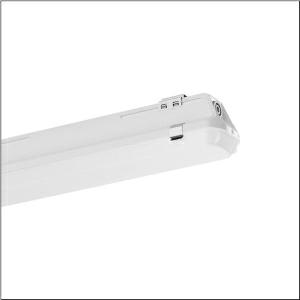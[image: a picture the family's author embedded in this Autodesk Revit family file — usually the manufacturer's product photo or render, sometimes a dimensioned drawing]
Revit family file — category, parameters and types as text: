
# Revit family: monsun_11_51fp108p430h
name_source: partatom
category: Lighting Fixtures
units: mm (PartAtom-declared; Revit-internal decimal feet)

## family parameters
Cut with Voids When Loaded = No
Host = Face
Light Source = No
Part Type = Normal
Room Calculation Point = No
Round Connector Dimension = Use Diameter
Shared = No

## types (1)
- Monsun 11 (1 x LED, 3970 lm, 22.2 W, 4000K)
    Apparent Load = 22 VA
    CIE Flux Codes = 47 77 93 94 100
    Color Rendering = 80
    Color Temperature = 4000K
    Default Elevation = 1800 mm
    Description = Monsun 11, damp-proof luminaire, chain hanger, primary optical cover: enclosure, of PMMA, light emission: direct distribution, primary light characteristic: symmetric, installation type: suspended mounting, surface-mounted, horizontal mounting, vertical mounting, LED, rated luminous flux: 3.970lm, luminous efficacy: 179lm/W, light colour: 840, colour temperature: 4000K, control gear: ON/OFF, with terminal, 3-pole, max. 2.5mm², mains connection: 220..240V, AC, 50/60Hz, rated input power: 22W, luminaire housing, of glass-fibre reinforced polyester, uncoated, bright grey, incl. chain hanger, length: 1.590mm, width: 90mm, height: 88mm, clip for enclosure, of stainless steel (V2A), ceiling mounting element, of stainless steel (V2A), chain hanger, of stainless steel (V2A), protection rating (complete): IP66, insulation class (complete): insulation class I (protective earthing), certification: CE, ENEC, VDE, UKCA, protection symbol: D, impact resistance: IK04, permissible operating ambient temperature: -35..+40°C, standard: EN 50419, EN 60598-2-1, no direct snow, no direct sun, no direct rain, for indoor or canopied outdoor use, corresponds to IFS (International Featured Standards) requirements for safety and quality in the food industry, contact your sales advisor before using the luminaires in applications with unclear chemical exposure, large temperature fluctuations or condensation-forming humidity, LABS conformity tested according to VDMA 24364:2018-05, packaging unit: 1 piece
    Height = 89 mm
    Lamp = 1 x LED
    Lamp Light Flux = 3970 lm
    Lamp Power = 22.2 W
    Lamp count = 1
    Length = 1590 mm
    Luminous efficacy = 179 lm/W
    Manufacturer = Siteco
    ModVariant = No
    Model = 51FP108P430H
    Mounting Place = Ceiling
    Mounting Type = Surface mounted
    Number of Poles = 1
    OnlyDefault = Yes
    Power Factor = 1
    Product Name = Monsun 11
    Product group = damp-proof luminaire
    ProductGroupID = 300
    Protection Class = Protection class I
    Protection Degree = IP 66
    RLX_Detail_Level = 1
    RLX_Emergency_Light_Flux = 0 lm
    RLX_Emergency_Type = 0
    RLX_Emergency_Type_DB = No
    RlxData = <blob elided: 88609 chars, md5=471f84ae>
    Socket = socket
    Standby Power = 0 W
    System Light Flux = 3970 lm
    System Power = 22 W
    Type Comments = Product without accessories
    Type Image = l_1349237.jpg
    URL = http://relux.com
    VarID = ---
    Voltage = 0 V
    Weight = 0.00 kg
    Width = 90 mm

## geometry (parser evidence)
native form markers: Blend x4, Sweep x13
no freeform markers — native parametric forms only
